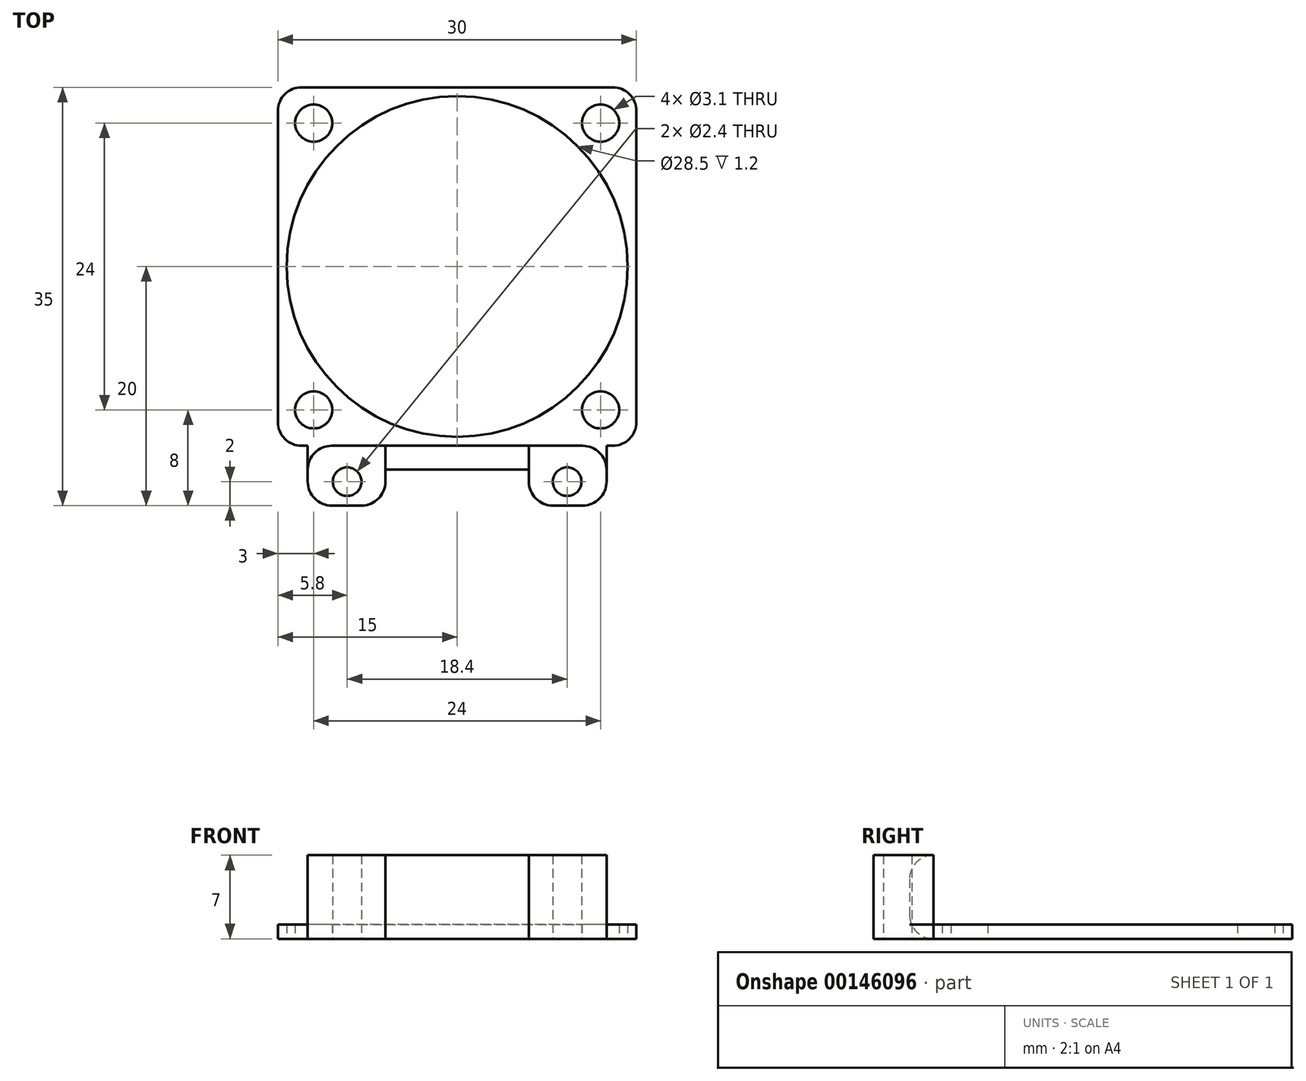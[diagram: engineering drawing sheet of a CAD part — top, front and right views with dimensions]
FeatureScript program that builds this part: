
annotation { "Feature Type Name" : "Feature", "Feature Type Description" : "" }
export const myFeature = defineFeature(function(context is Context, id is Id, definition is map)
    precondition{}
    {
        {
            var Q0;
            Q0=qCreatedBy(makeId("Top.planeOp"),FACE);
            var sketch = newSketch(context, id + "F0", { "sketchPlane" : qUnion([Q0])});
            skLineSegment(sketch, "E0.bottom", {"start": v(15, -15) * mm, "end": v(-15, -15) * mm});
            skLineSegment(sketch, "E0.top", {"start": v(15, 15) * mm, "end": v(-15, 15) * mm});
            skLineSegment(sketch, "E0.left", {"start": v(15, -15) * mm, "end": v(15, 15) * mm});
            skLineSegment(sketch, "E0.right", {"start": v(-15, -15) * mm, "end": v(-15, 15) * mm});
            skPoint(sketch, "E0.middle", {"position": v(0, 0) * mm});
            skLineSegment(sketch, "E1.bottom", {"start": v(12, -12) * mm, "end": v(-12, -12) * mm, "construction": true});
            skLineSegment(sketch, "E1.top", {"start": v(12, 12) * mm, "end": v(-12, 12) * mm, "construction": true});
            skLineSegment(sketch, "E1.left", {"start": v(12, -12) * mm, "end": v(12, 12) * mm, "construction": true});
            skLineSegment(sketch, "E1.right", {"start": v(-12, -12) * mm, "end": v(-12, 12) * mm, "construction": true});
            skCircle(sketch, "E2", {"center": v(-12, 12) * mm, "radius": 1.55 * mm});
            skCircle(sketch, "E3", {"center": v(12, 12) * mm, "radius": 1.55 * mm});
            skCircle(sketch, "E4", {"center": v(12, -12) * mm, "radius": 1.55 * mm});
            skCircle(sketch, "E5", {"center": v(-12, -12) * mm, "radius": 1.55 * mm});
            skLineSegment(sketch, "E6", {"start": v(-14.96, -20) * mm, "end": v(-6, -20) * mm, "construction": true});
            skLineSegment(sketch, "E7.bottom", {"start": v(-15, -15) * mm, "end": v(15, -15) * mm});
            skLineSegment(sketch, "E7.top", {"start": v(-6, -17) * mm, "end": v(6, -17) * mm});
            skLineSegment(sketch, "E8.bottom", {"start": v(-12.5, -15) * mm, "end": v(12.5, -15) * mm});
            skLineSegment(sketch, "E8.top", {"start": v(-12.5, -20) * mm, "end": v(-6, -20) * mm});
            skLineSegment(sketch, "E8.left", {"start": v(-12.5, -15) * mm, "end": v(-12.5, -20) * mm});
            skLineSegment(sketch, "E8.right", {"start": v(12.5, -15) * mm, "end": v(12.5, -20) * mm});
            skLineSegment(sketch, "E9.bottom", {"start": v(-6, -15) * mm, "end": v(6, -15) * mm});
            skLineSegment(sketch, "E9.left", {"start": v(-6, -15) * mm, "end": v(-6, -20) * mm});
            skLineSegment(sketch, "E9.right", {"start": v(6, -15) * mm, "end": v(6, -20) * mm});
            skPoint(sketch, "E7.right.end.orphan", {"position": v(15, -17) * mm});
            skLineSegment(sketch, "E10.trimOffspring", {"start": v(6, -20) * mm, "end": v(15.77, -20) * mm, "construction": true});
            skLineSegment(sketch, "E11.trimOffspring", {"start": v(6, -20) * mm, "end": v(12.5, -20) * mm});
            skLineSegment(sketch, "E12", {"start": v(-13.8, -18) * mm, "end": v(14.7, -18) * mm, "construction": true});
            skLineSegment(sketch, "E13", {"start": v(-9.2, -15) * mm, "end": v(-9.2, -21.94) * mm, "construction": true});
            skLineSegment(sketch, "E14", {"start": v(9.2, -15) * mm, "end": v(9.2, -21.94) * mm, "construction": true});
            skCircle(sketch, "E15", {"center": v(-9.2, -18) * mm, "radius": 1.2 * mm});
            skCircle(sketch, "E16", {"center": v(9.2, -18) * mm, "radius": 1.2 * mm});
            skCircle(sketch, "E17", {"center": v(0, 0) * mm, "radius": 14.25 * mm});
            skSolve(sketch);
        }
        {
            var Q0;
            Q0=makeQuery(id+"F0.imprint","IMPRINT",FACE,{"disambiguationData":[TD([[makeQuery(id+"F0.imprint","IMPRINT",EDGE,{"derivedFrom":sQuery(id+"F0.wireOp",EDGE,"E0.top")}),1.0]])]});
            var Q1;
            {var subQ4=sQuery(id+"F0.wireOp",EDGE,"E8.top");Q1=makeQuery(id+"F0.imprint","IMPRINT",FACE,{"disambiguationData":[TD([[makeQuery(id+"F0.imprint","IMPRINT",EDGE,{"derivedFrom":subQ4}),1.0]])]});}
            var Q2;
            {var subQ0=sQuery(id+"F0.wireOp",EDGE,"E7.top");Q2=makeQuery(id+"F0.imprint","IMPRINT",FACE,{"disambiguationData":[TD([[makeQuery(id+"F0.imprint","IMPRINT",EDGE,{"derivedFrom":subQ0}),1.0]])]});}
            var Q3;
            {var subQ5=sQuery(id+"F0.wireOp",EDGE,"E8.right");Q3=makeQuery(id+"F0.imprint","IMPRINT",FACE,{"disambiguationData":[TD([[makeQuery(id+"F0.imprint","IMPRINT",EDGE,{"derivedFrom":subQ5}),-1.0]])]});}
            extrude(context, id + "F1", {"entities" : qUnion([Q0, Q1, Q2, Q3]), "depth" : 1.2 * mm});
        }
        {
            var Q0;
            {var subQ0=sQuery(id+"F0.wireOp",EDGE,"E7.top");Q0=makeQuery(id+"F0.imprint","IMPRINT",FACE,{"disambiguationData":[TD([[makeQuery(id+"F0.imprint","IMPRINT",EDGE,{"derivedFrom":subQ0}),1.0]])]});}
            var Q1;
            {var subQ4=sQuery(id+"F0.wireOp",EDGE,"E8.top");Q1=makeQuery(id+"F0.imprint","IMPRINT",FACE,{"disambiguationData":[TD([[makeQuery(id+"F0.imprint","IMPRINT",EDGE,{"derivedFrom":subQ4}),1.0]])]});}
            var Q2;
            {var subQ5=sQuery(id+"F0.wireOp",EDGE,"E8.right");Q2=makeQuery(id+"F0.imprint","IMPRINT",FACE,{"disambiguationData":[TD([[makeQuery(id+"F0.imprint","IMPRINT",EDGE,{"derivedFrom":subQ5}),-1.0]])]});}
            extrude(context, id + "F2", {"entities" : qUnion([Q0, Q1, Q2]), "operationType" : NewBodyOperationType.ADD, "depth" : 7 * mm});
        }
        {
            var Q0;
            Q0=makeQuery(id+"F1.opExtrude","SWEPT_EDGE",EDGE,{"disambiguationData":[OSD([sQuery(id+"F0.wireOp",EDGE,"E0.left"),sQuery(id+"F0.wireOp",EDGE,"E7.bottom")])]});
            var Q1;
            Q1=makeQuery(id+"F1.opExtrude","SWEPT_EDGE",EDGE,{"disambiguationData":[OSD([sQuery(id+"F0.wireOp",EDGE,"E0.right"),sQuery(id+"F0.wireOp",EDGE,"E7.bottom")])]});
            var Q2;
            Q2=makeQuery(id+"F1.opExtrude","SWEPT_EDGE",EDGE,{"disambiguationData":[OSD([sQuery(id+"F0.wireOp",EDGE,"E0.top"),sQuery(id+"F0.wireOp",EDGE,"E0.right")])]});
            var Q3;
            Q3=makeQuery(id+"F1.opExtrude","SWEPT_EDGE",EDGE,{"disambiguationData":[OSD([sQuery(id+"F0.wireOp",EDGE,"E0.top"),sQuery(id+"F0.wireOp",EDGE,"E0.left")])]});
            var Q4;
            {var subQ0=sQuery(id+"F0.wireOp",EDGE,"E8.left");var subQ1=sQuery(id+"F0.wireOp",EDGE,"E8.top");Q4=makeQuery(id+"F2.boolean.opBoolean","MERGE",EDGE,{"derivedFrom":[makeQuery(id+"F1.opExtrude","SWEPT_EDGE",EDGE,{"disambiguationData":[OSD([subQ1,subQ0])]}),makeQuery(id+"F2.opExtrude","SWEPT_EDGE",EDGE,{"disambiguationData":[OSD([subQ1,subQ0])]})]});}
            var Q5;
            {var subQ0=sQuery(id+"F0.wireOp",EDGE,"E9.left");var subQ1=sQuery(id+"F0.wireOp",EDGE,"E8.top");Q5=makeQuery(id+"F2.boolean.opBoolean","MERGE",EDGE,{"derivedFrom":[makeQuery(id+"F1.opExtrude","SWEPT_EDGE",EDGE,{"disambiguationData":[OSD([subQ1,subQ0])]}),makeQuery(id+"F2.opExtrude","SWEPT_EDGE",EDGE,{"disambiguationData":[OSD([subQ1,subQ0])]})]});}
            var Q6;
            {var subQ0=sQuery(id+"F0.wireOp",EDGE,"E11.trimOffspring");var subQ1=sQuery(id+"F0.wireOp",EDGE,"E9.right");Q6=makeQuery(id+"F2.boolean.opBoolean","MERGE",EDGE,{"derivedFrom":[makeQuery(id+"F1.opExtrude","SWEPT_EDGE",EDGE,{"disambiguationData":[OSD([subQ1,subQ0])]}),makeQuery(id+"F2.opExtrude","SWEPT_EDGE",EDGE,{"disambiguationData":[OSD([subQ1,subQ0])]})]});}
            var Q7;
            {var subQ0=sQuery(id+"F0.wireOp",EDGE,"E11.trimOffspring");var subQ1=sQuery(id+"F0.wireOp",EDGE,"E8.right");Q7=makeQuery(id+"F2.boolean.opBoolean","MERGE",EDGE,{"derivedFrom":[makeQuery(id+"F1.opExtrude","SWEPT_EDGE",EDGE,{"disambiguationData":[OSD([subQ1,subQ0])]}),makeQuery(id+"F2.opExtrude","SWEPT_EDGE",EDGE,{"disambiguationData":[OSD([subQ1,subQ0])]})]});}
            var Q8;
            Q8=makeQuery(id+"F2.opExtrude","SWEPT_EDGE",EDGE,{"disambiguationData":[OSD([sQuery(id+"F0.wireOp",EDGE,"E7.bottom"),sQuery(id+"F0.wireOp",EDGE,"E8.bottom"),sQuery(id+"F0.wireOp",EDGE,"E8.right")])]});
            var Q9;
            Q9=makeQuery(id+"F2.opExtrude","SWEPT_EDGE",EDGE,{"disambiguationData":[OSD([sQuery(id+"F0.wireOp",EDGE,"E7.bottom"),sQuery(id+"F0.wireOp",EDGE,"E8.bottom"),sQuery(id+"F0.wireOp",EDGE,"E8.left")])]});
            var Q10;
            Q10=makeQuery(id+"F2.opExtrude","CAP_EDGE",EDGE,{"disambiguationData":[OSD([sQuery(id+"F0.wireOp",EDGE,"E7.top")])],"isStart":false});
            var Q11;
            Q11=makeQuery(id+"F1.opExtrude","CAP_EDGE",EDGE,{"disambiguationData":[OSD([sQuery(id+"F0.wireOp",EDGE,"E7.top")])],"isStart":true});
            fillet(context, id + "F3", {"entities" : qUnion([Q0, Q1, Q2, Q3, Q4, Q5, Q6, Q7, Q8, Q9, Q10, Q11]), "radius" : 2 * mm, "tangentPropagation" : true, "allowEdgeOverflow" : false});
        }
    });
